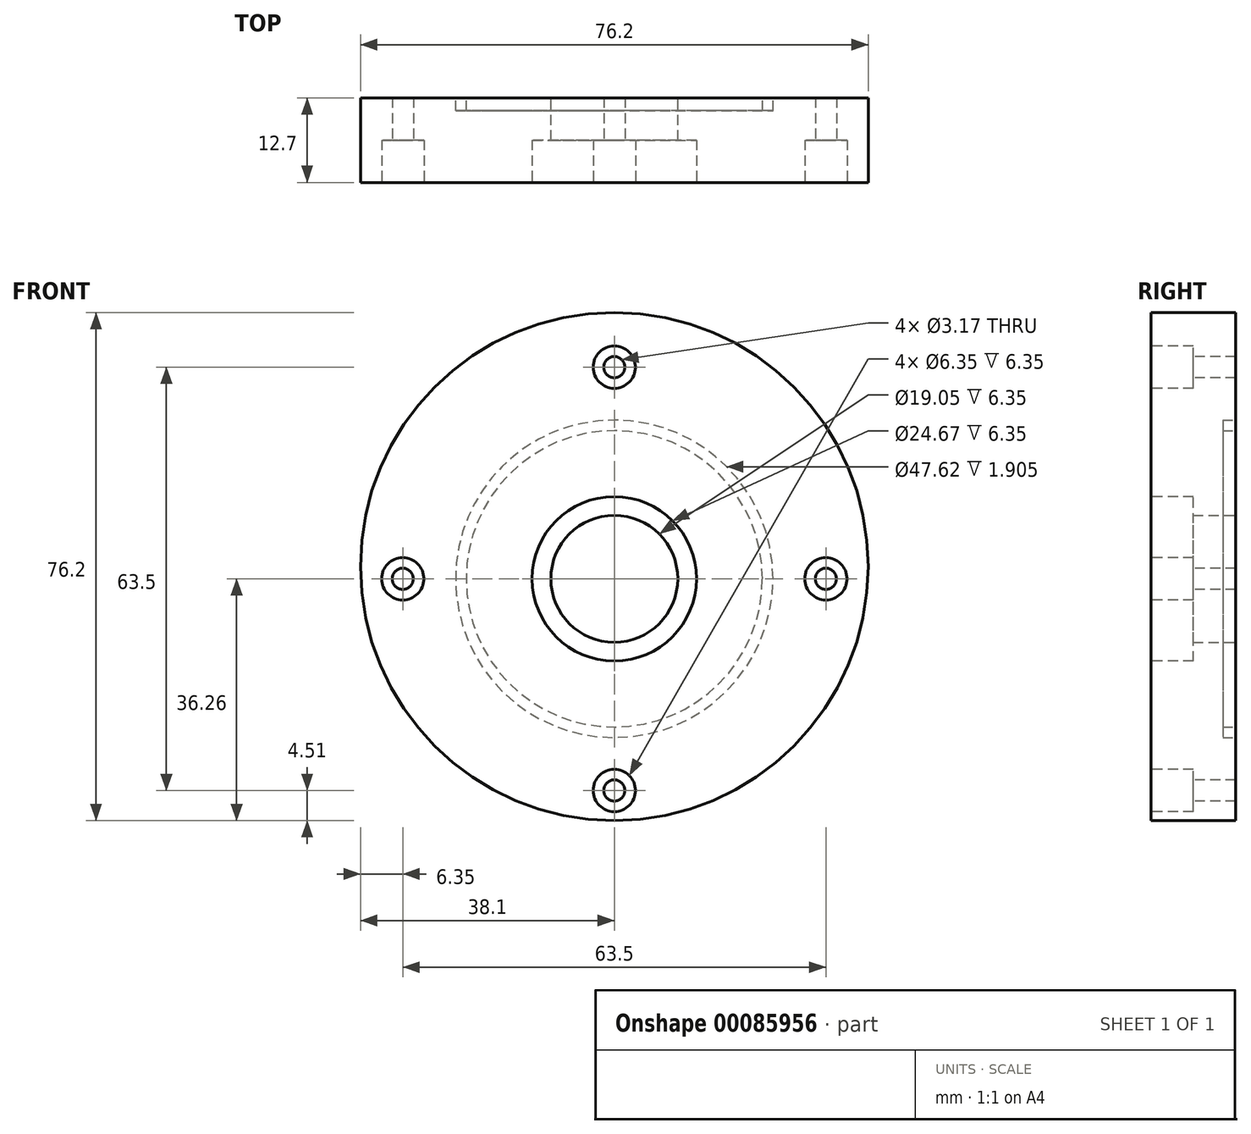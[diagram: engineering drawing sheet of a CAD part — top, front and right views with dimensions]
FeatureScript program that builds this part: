
annotation { "Feature Type Name" : "Feature", "Feature Type Description" : "" }
export const myFeature = defineFeature(function(context is Context, id is Id, definition is map)
    precondition{}
    {
        {
            var Q0;
            Q0=qCreatedBy(makeId("Front.planeOp"),FACE);
            var sketch = newSketch(context, id + "F0", { "sketchPlane" : qUnion([Q0])});
            skCircle(sketch, "E0", {"center": v(0, 1.84) * mm, "radius": 38.1 * mm});
            skCircle(sketch, "E1", {"center": v(0, 0) * mm, "radius": 9.53 * mm});
            skSolve(sketch);
        }
        {
            var Q0;
            Q0 = qSketchRegion(id + "F0", true);
            extrude(context, id + "F1", {"entities" : qUnion([Q0]), "depth" : 12.7 * mm});
        }
        {
            var Q0;
            Q0=makeQuery(id+"F1.opExtrude","CAP_FACE",FACE,{"disambiguationData":[OSD([sQuery(id+"F0.wireOp",EDGE,"bdmzsmJ8-bhNa-m4m3-Temb-lQKyfwYFkQNE"),sQuery(id+"F0.wireOp",EDGE,"E0")])],"isStart":false});
            var sketch = newSketch(context, id + "F2", { "sketchPlane" : qUnion([Q0])});
            skCircle(sketch, "E2", {"center": v(0, 0) * mm, "radius": 12.33 * mm});
            skSolve(sketch);
        }
        {
            var Q0;
            Q0 = qSketchRegion(id + "F2", true);
            extrude(context, id + "F3", {"entities" : qUnion([Q0]), "operationType" : NewBodyOperationType.REMOVE, "oppositeDirection" : true, "depth" : 6.35 * mm});
        }
        {
            var Q0;
            Q0=makeQuery(id+"F1.opExtrude","CAP_FACE",FACE,{"disambiguationData":[OSD([sQuery(id+"F0.wireOp",EDGE,"E0"),sQuery(id+"F0.wireOp",EDGE,"E1")])],"isStart":false});
            var sketch = newSketch(context, id + "F4", { "sketchPlane" : qUnion([Q0])});
            skPoint(sketch, "E3", {"position": v(0, 31.75) * mm});
            skPoint(sketch, "E4", {"position": v(31.75, 0) * mm});
            skPoint(sketch, "E5", {"position": v(0, -31.75) * mm});
            skPoint(sketch, "E6", {"position": v(-31.75, 0) * mm});
            skSolve(sketch);
        }
        {
            var Q0;
            Q0=sQuery(id+"F4.wireOp",VERTEX,"E3");
            var Q1;
            Q1=sQuery(id+"F4.wireOp",VERTEX,"E4");
            var Q2;
            Q2=sQuery(id+"F4.wireOp",VERTEX,"E5");
            var Q3;
            Q3=sQuery(id+"F4.wireOp",VERTEX,"E6");
            var Q4;
            Q4=makeQuery(id+"F1.opExtrude","SWEPT_BODY",BODY,{"disambiguationData":[OSD([sQuery(id+"F0.wireOp",EDGE,"E0"),sQuery(id+"F0.wireOp",EDGE,"E1")])]});
            hole(context, id + "F5", {"style" : HoleStyle.C_BORE, "endStyle" : HoleEndStyle.THROUGH, "holeDiameter" : 3.17 * mm, "cBoreDiameter" : 6.35 * mm, "cBoreDepth" : 6.35 * mm, "locations" : qUnion([Q0, Q1, Q2, Q3]), "scope" : qUnion([Q4]), "isTappedThrough" : true});
        }
        {
            var Q0;
            Q0=makeQuery(id+"F1.opExtrude","CAP_FACE",FACE,{"disambiguationData":[OSD([sQuery(id+"F0.wireOp",EDGE,"E0"),sQuery(id+"F0.wireOp",EDGE,"E1")])],"isStart":true});
            var sketch = newSketch(context, id + "F6", { "sketchPlane" : qUnion([Q0])});
            skCircle(sketch, "E7", {"center": v(0, 0) * mm, "radius": 22.23 * mm});
            skCircle(sketch, "E8", {"center": v(0, 0) * mm, "radius": 23.81 * mm});
            skSolve(sketch);
        }
        {
            var Q0;
            Q0 = qSketchRegion(id + "F6", true);
            extrude(context, id + "F7", {"entities" : qUnion([Q0]), "operationType" : NewBodyOperationType.REMOVE, "oppositeDirection" : true, "depth" : 1.9 * mm});
        }
    });
